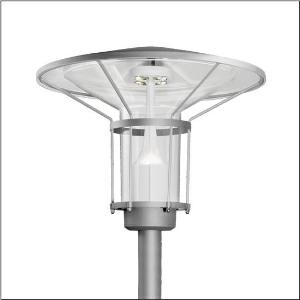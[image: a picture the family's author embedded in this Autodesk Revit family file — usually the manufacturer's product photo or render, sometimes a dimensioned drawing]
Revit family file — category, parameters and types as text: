
# Revit family: laterne_classic_iq___p1_0a_5xa5245bf14hp_df6d
name_source: partatom
category: Lighting Fixtures
units: mm (PartAtom-declared; Revit-internal decimal feet)

## family parameters
Cut with Voids When Loaded = No
Host = Face
Light Source = No
Part Type = Normal
Room Calculation Point = No
Round Connector Dimension = Use Diameter
Shared = No

## types (1)
- --- (1 x LED, 3480 lm, 33.6 W, 2200K)
    Apparent Load = 34 VA
    CIE Flux Codes = 31 61 91 96 100
    Color Rendering = 70
    Color Temperature = 2200K
    Default Elevation = 1800 mm
    Description = Lantern Classic iQ, mast luminaire, Module 540 iQ-SR, primary light control with 3 zone facetted reflector, of plastic, silver coated, highly specular, structured, primary optical cover: cover, of PMMA, transparent, light distribution: P1.0a, light emission: direct distribution, primary light characteristic: strongly asymmetric, installation type: post-top, LED, High Power LED, rated luminous flux: 3.480lm, luminous efficacy: 104lm/W, light colour: 722, colour temperature: 2200K, control gear: ECG iQ, control: presetting dimming logarithmic, Street-Remote, Auto-Match, Temp-Guard, Lumen-Switch, Night-Set, Smart-Wire, Light-Fading, Desk-Remote (wireless, voltage-free reading and setting of iQ features in the workshop via application-optimized NFC function/RFID function), optimised constant luminous flux control (CLO 2.0), with terminal, 6-pole, max. 2.5mm², mains connection: 230..240V, AC, 50/60Hz, start of lifetime: 34W, end of service life: 36W, reduction: 15W, luminaire housing, upper part, of glass-fibre reinforced polyester, coated, Siteco® metallic grey (DB 702S), diameter: 750mm, height: 596mm, spigot size: d x l = 76 x 70mm (post-top) | with reducer (optional accessory) 60 x 70mm, post-top mast mounting element, of diecast aluminium, coated, Siteco® metallic grey (DB 702S), Module 540 iQ-SR, traffic white (RAL 9016), equipment: Power, protection rating (complete): IP65, insulation class (complete): insulation class II (safety insulation), certification: CE, ENEC, VDE, packaging unit: 1 piece

Light Distribution: P1.0a
    Height = 596 mm
    Lamp = 1 x LED
    Lamp Light Flux = 3480 lm
    Lamp Power = 33.6 W
    Lamp count = 1
    Length = 750 mm
    Luminous efficacy = 104 lm/W
    Manufacturer = Siteco
    ModVariant = No
    Model = 5XA5245BF14HP
    Number of Poles = 1
    OnlyDefault = Yes
    Power Factor = 1
    Product Name = Laterne Classic iQ | P1.0a
    Product group = mast luminaire | pylon top
    ProductGroupID = 6100
    Protection Class = Protection class II
    Protection Degree = IP 65
    RLX_Detail_Level = 1
    RLX_Emergency_Light_Flux = 0 lm
    RLX_Emergency_Type = 0
    RLX_Emergency_Type_DB = No
    RlxData = <blob elided: 65345 chars, md5=e3b8ad2a>
    Socket = socket
    Standby Power = 0 W
    System Light Flux = 3480 lm
    System Power = 34 W
    Type Comments = factory setting: luminous flux: 100 % | dim-lin: 254 | 695 mA
    Type Image = l_1006052.jpg
    URL = http://relux.com
    VarID = @adj_145847
    Voltage = 0 V
    Weight = 0.00 kg
    Width = 0 mm  [stored 0 ft]

note: [stored X ft] marks values corroborated as IEEE doubles in the binary element streams (Revit-internal decimal feet)

## geometry (parser evidence)
native form markers: Blend x4, Sweep x11
no freeform markers — native parametric forms only
